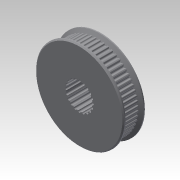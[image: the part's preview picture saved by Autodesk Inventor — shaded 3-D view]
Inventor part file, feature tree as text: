
AUTODESK INVENTOR PART (.ipt)
format: ipt  version: 2020 (Build 240168000, 168)  size: 588,800 bytes
history: native  units: mm
features: extrude x2, sketch x2, revolve x1, fillet x1, pattern_circular x1, chamfer x1
ambient origin geometry x8: Origin, YZ Plane, XZ Plane, XY Plane, X Axis, Y Axis, Z Axis, Center Point
bodies: Solid1 (feature_tree)
feature tree (8):
  revolve  "Revolution1"  [1 undecoded]
  extrude  "Extrusion1"  Depth=0.3mm TaperAngle=360.0deg
  fillet  "Fillet1"  Radius=18.85mm
  pattern_circular  "Circular Pattern1"  [2 undecoded]
  chamfer  "Chamfer2"  Distance=7.5mm
  extrude  "Extrusion4"  Depth=0.3mm
  sketch  "Sketch2"  dims[d7=90.0deg d8=1.1mm]
  sketch  "Sketch6"  dims[d10=10.0mm d11=0.0mm d12=600.0mm d13=360.0deg d18=18.85mm d19=0.3mm d20=7.5mm d21=1.0mm d22=1.5mm d23=0.5mm d24=120.0deg d25=4.0mm d26=18.85mm d43=0.5mm d44=2.0mm d45=45.0deg d46=0.5mm d47=0.5mm d48=135.0deg d53=12.0mm d54=1.2mm d55=200.0mm d57=360.0deg d59=12.25mm d60=0.0mm d37=0.5mm d38=0.872665mm d39=0.5mm d40=0.872665mm]
note: 3 required parameter values undecoded (feature->parameter linkage not recoverable at this tier; creation-order binding heuristic only, values carry confidence <= 0.55)